# Revit family: Broan®_AI_Series™-Heat_Recovery_High_CFM_Ventilator_(HRV)-Top_Port
name_source: partatom
category: Mechanical Equipment
units: mm (PartAtom-declared; Revit-internal decimal feet)

## family parameters
Always vertical = No
Classification = None
Cut with Voids When Loaded = No
Part Type = Normal
Room Calculation Point = No
Round Connector Dimension = Use Diameter
Shared = No
Work Plane-Based = Yes

## types (2) — shared parameters
Default Elevation = 0.00"
Exhaust Air Connection Diameter = 6"
Frequency = 60 Hz
Height = 21.69"
Length = 21.00"
Manufacturer = Broan
Number of Poles = 1
Operating Weight = 47.00 lb
Phase = 1
Product Documentation Link = https://www.broan-nutone.com
Product Page URL = https://www.broan-nutone.com
Requirements and Standards = UL 1812
CSA C439
ROHS 2015/863
Prop 65
Return Air Connection Diameter = 6"
Supply Air Connection Diameter = 6"
URL = https://www.broan-nutone.com
Voltage = 120 V
Width = 24.81"
c Back Clearance = 0.00"
c Front Clearance = 8.00"
c Gen Diameter = 6.00"
c Height = 19.13"
c Left Clearance = 0.00"
c MC width = 14.50"
c Offset vent side = 5.00"
c Right Clrearance = 0.00"
c Top Clearance = 9.00"
c Vent Height = 2.56"
c Width = 21.88"
c Width MC = 2.93"
zero-valued in all types: Power Factor

## per-type parameters (varying)
| type | Air Volume | Fan Wattage | Model | Noise | Product Name | c Constraints |
| Broan®_AI_Series™-180_CFM-Heat_Recovery_Ventilator_(HRV)-Top_Port-78%_eff | 180 CFM | 70 W | B180H75RT | 110 | Broan® AI Series™ 180 CFM Heat Recovery Ventilator (HRV) | 1 |
| Broan®_AI_Series™-210_CFM-Heat_Recovery_Ventilator_(HRV)-Top_Port-78%_eff | 210 CFM | 73 W | B230H75RT | 163 | Broan® AI Series™ 230 CFM Heat Recovery Ventilator (HRV) | 2 |

## geometry (parser evidence)
native form markers: Sweep x8
no freeform markers — native parametric forms only
